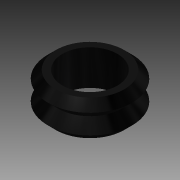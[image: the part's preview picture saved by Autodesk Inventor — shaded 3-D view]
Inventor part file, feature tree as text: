
AUTODESK INVENTOR PART (.ipt)
format: ipt  version: 2014 SP1 (Build 180222100, 222)  size: 95,744 bytes
history: native  units: in
note: dims shown in document units (in); Inventor stores cm internally (conversion verified against a paired STEP export)
features: revolve x1, sketch x1
ambient origin geometry x8: Origin, YZ Plane, XZ Plane, XY Plane, X Axis, Y Axis, Z Axis, Center Point
bodies: Solid1 (feature_tree)
feature tree (2):
  revolve  "Revolution1"  [1 undecoded]
  sketch  "Sketch1"  dims[d0=0.4028in d1=0.6289in d2=90.0deg d4=90.0deg d5=0.9602in d6=90.0deg]
note: 1 required parameter value undecoded (feature->parameter linkage not recoverable at this tier; creation-order binding heuristic only, values carry confidence <= 0.55)
